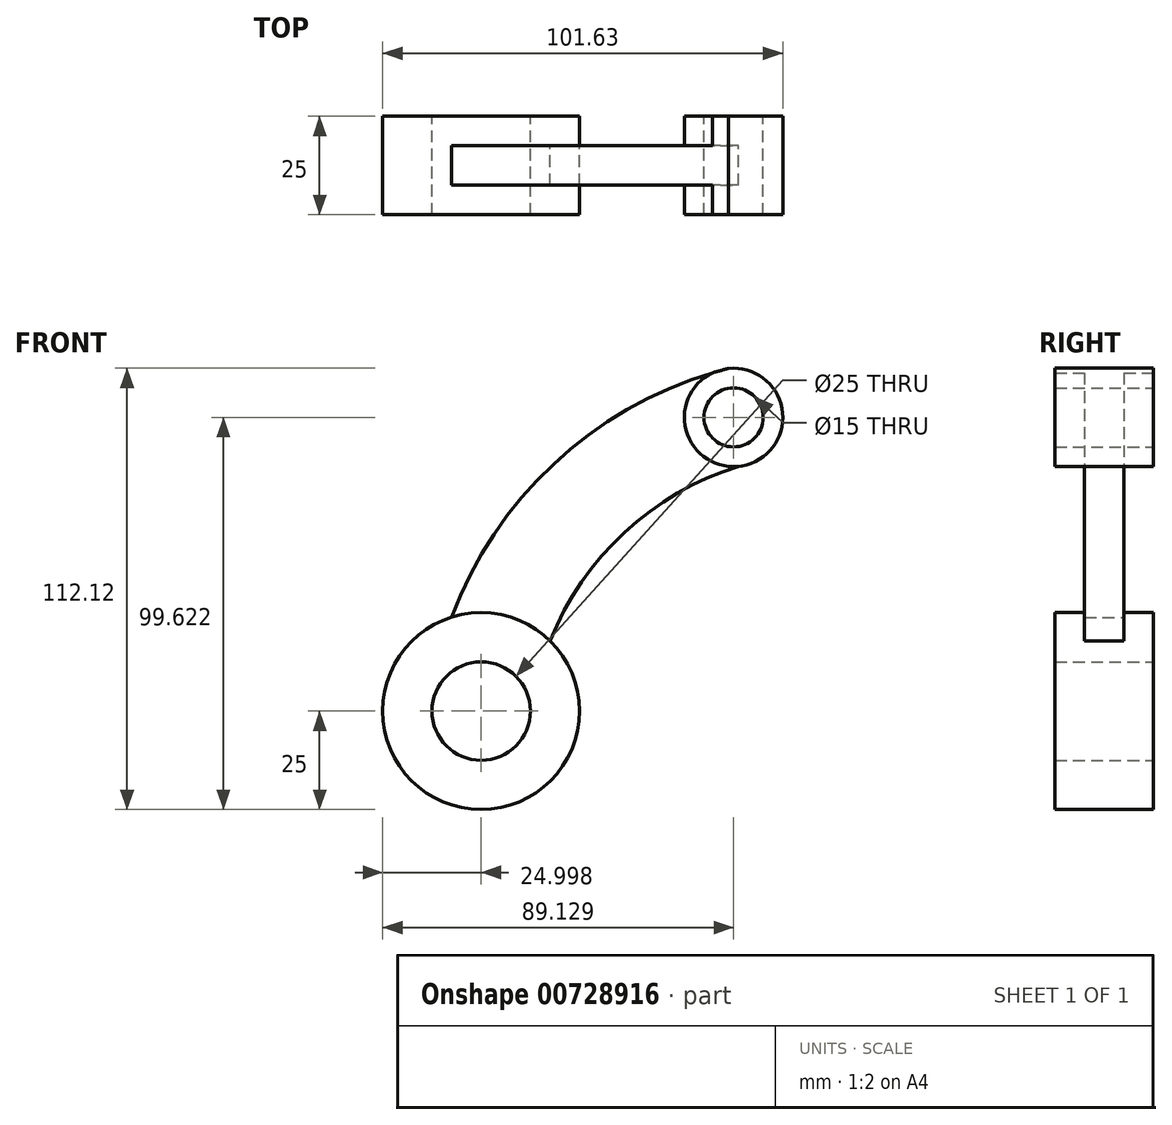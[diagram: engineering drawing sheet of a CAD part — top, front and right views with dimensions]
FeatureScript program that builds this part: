
annotation { "Feature Type Name" : "Feature", "Feature Type Description" : "" }
export const myFeature = defineFeature(function(context is Context, id is Id, definition is map)
    precondition{}
    {
        {
            var Q0;
            Q0=qCreatedBy(makeId("Front.planeOp"),FACE);
            var sketch = newSketch(context, id + "F0", { "sketchPlane" : qUnion([Q0])});
            skCircle(sketch, "E0", {"center": v(-109.41, 0) * mm, "radius": 25 * mm});
            skCircle(sketch, "E1", {"center": v(-109.41, 0) * mm, "radius": 12.5 * mm});
            skCircle(sketch, "E2", {"center": v(-45.28, 74.62) * mm, "radius": 12.5 * mm});
            skCircle(sketch, "E3", {"center": v(-45.28, 74.62) * mm, "radius": 7.5 * mm});
            skArc(sketch, "E4", {"start": v(-44.04, 62.18) * mm, "mid": v(-72.99, 45.42) * mm, "end": v(-91.87, 17.82) * mm});
            skArc(sketch, "E5", {"start": v(-46.52, 87.06) * mm, "mid": v(-89.52, 64.12) * mm, "end": v(-116.94, 23.84) * mm});
            skSolve(sketch);
        }
        {
            var Q0;
            {var subQ0=sQuery(id+"F0.wireOp",EDGE,"E4");Q0=makeQuery(id+"F0.imprint","IMPRINT",FACE,{"disambiguationData":[TD([[makeQuery(id+"F0.imprint","IMPRINT",EDGE,{"derivedFrom":subQ0}),-1.0]])]});}
            extrude(context, id + "F1", {"entities" : qUnion([Q0]), "endBound" : BoundingType.SYMMETRIC, "depth" : 10 * mm, "offsetDistance" : 25 * mm});
        }
        {
            var Q0;
            Q0=makeQuery(id+"F0.imprint","IMPRINT",FACE,{"disambiguationData":[TD([[makeQuery(id+"F0.imprint","IMPRINT",EDGE,{"derivedFrom":sQuery(id+"F0.wireOp",EDGE,"E1")}),-1.0]])]});
            var Q1;
            Q1=makeQuery(id+"F0.imprint","IMPRINT",FACE,{"disambiguationData":[TD([[makeQuery(id+"F0.imprint","IMPRINT",EDGE,{"derivedFrom":sQuery(id+"F0.wireOp",EDGE,"E3")}),-1.0]])]});
            extrude(context, id + "F2", {"entities" : qUnion([Q0, Q1]), "operationType" : NewBodyOperationType.ADD, "endBound" : BoundingType.SYMMETRIC, "depth" : 25 * mm, "offsetDistance" : 25 * mm});
        }
    });
